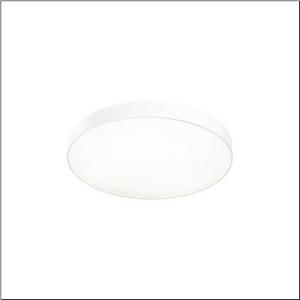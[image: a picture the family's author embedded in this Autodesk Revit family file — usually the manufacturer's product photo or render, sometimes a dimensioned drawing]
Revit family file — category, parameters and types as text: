
# Revit family: round_21_m_51mr36gd0321w
name_source: partatom
category: Lighting Fixtures
units: mm (PartAtom-declared; Revit-internal decimal feet)

## family parameters
Cut with Voids When Loaded = No
Host = Face
Light Source = No
Part Type = Normal
Room Calculation Point = No
Round Connector Dimension = Use Diameter
Shared = No

## types (1)
- Round 21 M (1 x LED, 7550 lm, 54.6 W, 3000K)
    Apparent Load = 55 VA
    CIE Flux Codes = 49 80 96 85 100
    Color Rendering = 80
    Color Temperature = 3000K
    Default Elevation = 1800 mm
    Description = Round 21 M, wall and ceiling luminaire, primary optical cover: cover, of PMMA, opal, light emission: direct/indirect distribution, primary light characteristic: symmetric, installation type: suspended mounting, surface-mounted, LED, rated luminous flux: 7.550lm, luminous efficacy: 138lm/W, light colour: 830, colour temperature: 3000K, control gear: DALI 2, with terminal, 5-pole, mains connection: 230V, AC, 50/60Hz, rated input power: 54.6W, housing, of aluminium, coated, white, diameter: 600mm, height: 62mm, protection rating (complete): IP40, insulation class (complete): insulation class I (protective earthing), certification: CE, impact resistance: IK04, permissible operating ambient temperature: -10..+35°C, packaging unit: 1 piece
    Height = 87 mm
    Lamp = 1 x LED
    Lamp Light Flux = 7550 lm
    Lamp Power = 54.6 W
    Lamp count = 1
    Length = 600 mm
    Luminous efficacy = 138 lm/W
    Manufacturer = Siteco
    ModVariant = No
    Model = 51MR36GD0321W
    Mounting Place = Ceiling
    Mounting Type = Surface mounted
    Number of Poles = 1
    OnlyDefault = Yes
    Power Factor = 1
    Product Name = Round 21 M
    Product group = wall and ceiling luminaire
    ProductGroupID = 304
    Protection Class = Protection class I
    Protection Degree = IP 40
    RLX_Detail_Level = 1
    RLX_Emergency_Light_Flux = 0 lm
    RLX_Emergency_Type = 0
    RLX_Emergency_Type_DB = No
    RlxData = <blob elided: 12125 chars, md5=bbe7e25e>
    Socket = socket
    Standby Power = 0 W
    System Light Flux = 7550 lm
    System Power = 55 W
    Type Comments = Product without accessories
    Type Image = l_1258330.jpg
    URL = http://relux.com
    VarID = ---
    Voltage = 0 V
    Weight = 0.00 kg
    Width = 0 mm  [stored 0 ft]

note: [stored X ft] marks values corroborated as IEEE doubles in the binary element streams (Revit-internal decimal feet)

## geometry (parser evidence)
native form markers: Sweep x11
no freeform markers — native parametric forms only
